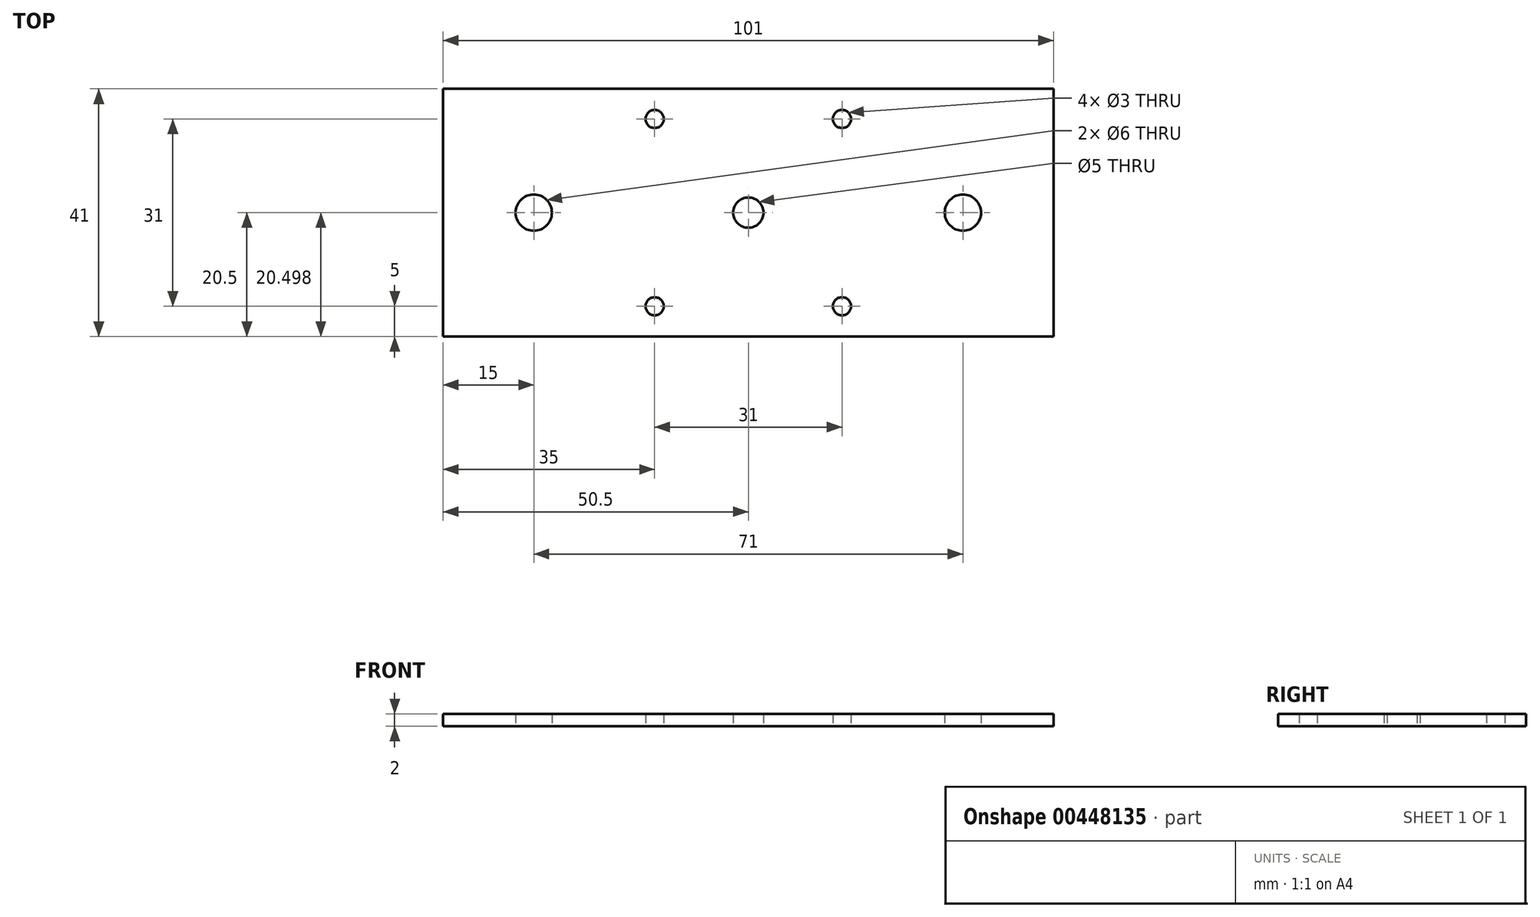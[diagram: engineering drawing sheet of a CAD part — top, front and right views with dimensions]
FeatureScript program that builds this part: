
annotation { "Feature Type Name" : "Feature", "Feature Type Description" : "" }
export const myFeature = defineFeature(function(context is Context, id is Id, definition is map)
    precondition{}
    {
        {
            var Q0;
            Q0=qCreatedBy(makeId("Top.planeOp"),FACE);
            var sketch = newSketch(context, id + "F0", { "sketchPlane" : qUnion([Q0])});
            skLineSegment(sketch, "E0.bottom", {"start": v(50.5, -20.5) * mm, "end": v(-50.5, -20.5) * mm});
            skLineSegment(sketch, "E0.top", {"start": v(50.5, 20.5) * mm, "end": v(-50.5, 20.5) * mm});
            skLineSegment(sketch, "E0.left", {"start": v(50.5, -20.5) * mm, "end": v(50.5, 20.5) * mm});
            skLineSegment(sketch, "E0.right", {"start": v(-50.5, -20.5) * mm, "end": v(-50.5, 20.5) * mm});
            skPoint(sketch, "E0.middle", {"position": v(0, 0) * mm});
            skCircle(sketch, "E1", {"center": v(-15.5, -15.5) * mm, "radius": 1.5 * mm});
            skCircle(sketch, "E2", {"center": v(-15.5, 15.5) * mm, "radius": 1.5 * mm});
            skCircle(sketch, "E3", {"center": v(15.5, 15.5) * mm, "radius": 1.5 * mm});
            skCircle(sketch, "E4", {"center": v(15.5, -15.5) * mm, "radius": 1.5 * mm});
            skCircle(sketch, "E5", {"center": v(-35.5, 0) * mm, "radius": 3 * mm});
            skCircle(sketch, "E6", {"center": v(35.5, 0) * mm, "radius": 3 * mm});
            skCircle(sketch, "E7", {"center": v(0, 0) * mm, "radius": 2.5 * mm});
            skSolve(sketch);
        }
        {
            var Q0;
            Q0=makeQuery(id+"F0.imprint","IMPRINT",FACE,{"disambiguationData":[TD([[makeQuery(id+"F0.imprint","IMPRINT",EDGE,{"derivedFrom":sQuery(id+"F0.wireOp",EDGE,"E0.bottom")}),-1.0]])]});
            extrude(context, id + "F1", {"entities" : qUnion([Q0]), "flatOperationType" : FlatOperationType.REMOVE, "offsetDistance" : 25.4 * mm, "depth" : 2 * mm, "domain" : OperationDomain.MODEL});
        }
    });
